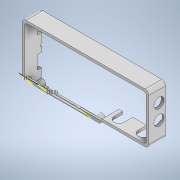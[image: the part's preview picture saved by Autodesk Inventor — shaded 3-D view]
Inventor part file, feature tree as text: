
AUTODESK INVENTOR PART (.ipt)
format: ipt  version: 2021 (Build 250183000, 183)  size: 572,928 bytes
history: native  units: mm
features: sketch x26, extrude x24, fillet x5, chamfer x5, hole x1
ambient origin geometry x8: Origin, YZ Plane, XZ Plane, XY Plane, X Axis, Y Axis, Z Axis, Center Point
bodies: Solid1 (feature_tree)
feature tree (61):
  extrude  "Extrusion1"  Depth=100.0mm
  extrude  "Extrusion3"  Depth=50.0mm
  extrude  "Extrusion4"  Depth=12.5mm
  extrude  "Extrusion12"  Depth=3.0mm TaperAngle=0.0deg
  extrude  "Extrusion13"  Depth=3.0mm TaperAngle=0.0deg
  fillet  "Fillet3"  Radius=2.0mm
  extrude  "Extrusion15"  Depth=2.0mm
  extrude  "Extrusion20"  Depth=1.2mm
  extrude  "Extrusion21"  Depth=12.0mm TaperAngle=0.0deg
  extrude  "Extrusion22"  Depth=2.0mm
  extrude  "Extrusion23"  Depth=3.0mm
  extrude  "Extrusion26"  Depth=4.4mm TaperAngle=0.0deg
  hole  "Hole2"  [1 undecoded]
  chamfer  "Chamfer6"  Distance=12.0mm
  chamfer  "Chamfer7"  Distance=12.0mm
  extrude  "Extrusion27"  Depth=8.0mm
  fillet  "Fillet4"  Radius=8.0mm
  extrude  "Extrusion28"  Depth=2.0mm TaperAngle=0.0deg
  extrude  "Extrusion29"  Depth=12.0mm
  extrude  "Extrusion30"  Depth=8.0mm
  fillet  "Fillet5"  Radius=8.0mm
  extrude  "Extrusion34"  Depth=2.0mm TaperAngle=0.0deg
  extrude  "Extrusion35"  Depth=3.0mm
  extrude  "Extrusion36"  Depth=50.0mm
  extrude  "Extrusion37"  Depth=3.0mm
  fillet  "Fillet6"  Radius=3.0mm
  extrude  "Extrusion38"  Depth=3.0mm
  extrude  "Extrusion39"  Depth=4.8mm
  chamfer  "Chamfer8"  Distance=6.0mm
  extrude  "Extrusion40"  Depth=2.0mm TaperAngle=45.0deg
  fillet  "Fillet7"  Radius=0.8mm
  extrude  "Extrusion41"  Depth=0.5mm
  chamfer  "Chamfer9"  Distance=2.0mm
  chamfer  "Chamfer10"  Distance=2.0mm
  extrude  "Extrusion42"  Depth=2.0mm
  sketch  "Sketch47"  dims[d158=4.8mm d159=6.0mm d160=0.0mm d161=2.0mm d162=6.0mm d163=4.0mm d164=2.0mm d165=90.0deg d166=4.0mm d167=20.594885mm d177=2.0mm d178=2.0mm d179=45.0deg d180=0.8mm d181=2.0mm d182=45.0deg d184=68.0mm d189=2.0mm d190=0.0mm d191=2.0mm d192=2.0mm d193=24.0mm d194=2.0mm d195=0.0mm d196=36.5mm d197=46.5mm d198=3.5mm d199=2.0mm d200=0.0mm d201=12.5mm d202=23.0mm d203=3.5mm d204=2.0mm d205=0.0mm d206=1.0mm d217=7.6mm d218=10.0mm d219=46.4mm d220=20.0mm d221=0.0mm d222=22.68928mm d223=67.0mm d224=0.0mm d225=1.2mm d226=0.0mm d227=1.2mm d228=0.0mm d229=3.0mm d230=12.3mm d231=33.2mm d232=1.0mm d233=10.0mm d234=1.2mm d235=0.0mm d236=1.2mm d237=5.0mm d238=20.0mm d239=1.5mm d240=0.0mm d241=1.5mm d242=2.0mm d243=45.0deg d245=1.2mm d246=0.0mm d247=2.0mm d248=5.0mm d249=0.0mm d250=0.8mm d251=2.0mm d252=45.0deg d253=0.6mm d254=2.0mm d255=45.0deg d256=5.0mm d257=0.0mm d258=2.0mm d259=0.0mm d262=12.0mm d263=33.2mm d67=0.5mm d68=0.872665mm d69=0.5mm d70=0.872665mm d71=0.5mm d72=0.872665mm d73=0.5mm d74=0.872665mm d75=0.872665mm d76=0.5mm d77=0.872665mm d208=0.5mm d209=0.872665mm d210=0.5mm d211=0.872665mm d264=0.5mm d265=0.872665mm]
  sketch  "Sketch1"  dims[d0=52.0mm d1=100.0mm]
  sketch  "Sketch4"  dims[d2=26.0mm d3=50.0mm]
  sketch  "Sketch5"  dims[d4=1.2mm d5=0.0mm d35=12.5mm]
  sketch  "Sketch13"  dims[d36=63.1mm d37=3.0mm d38=0.0mm]
  sketch  "Sketch14"  dims[d39=50.673mm d40=3.0mm d41=0.0mm d79=2.0mm]
  sketch  "Sketch16"  dims[d80=2.0mm d81=2.0mm]
  sketch  "Sketch21"  dims[d82=1.2mm d83=44.0mm]
  sketch  "Sketch22"  dims[d84=59.0mm d85=12.0mm d86=0.0mm]
  sketch  "Sketch23"  dims[d87=2.0mm d88=12.6mm]
  sketch  "Sketch24"  dims[d89=12.0mm d90=0.0mm d91=3.0mm]
  sketch  "Sketch27"  dims[d95=33.8mm d96=4.4mm d97=0.0mm]
  sketch  "Sketch28"  dims[d117=2.0mm d118=2.0mm d119=12.0mm d120=0.0mm d121=12.0mm d122=0.0mm]
  sketch  "Sketch29"  dims[d123=70.0mm d124=89.0mm d125=8.0mm]
  sketch  "Sketch30"  dims[d126=8.0mm d127=2.0mm d128=0.0mm]
  sketch  "Sketch31"  dims[d129=8.0mm d130=12.0mm]
  sketch  "Sketch32"  dims[d131=12.0mm d132=8.0mm d133=8.0mm]
  sketch  "Sketch36"  dims[d134=8.0mm d135=2.0mm d136=0.0mm]
  sketch  "Sketch37"  dims[d144=3.0mm d145=3.0mm]
  sketch  "Sketch38"  dims[d146=3.0mm d147=50.0mm]
  sketch  "Sketch39"  dims[d148=97.0mm d149=15.0mm d150=3.0mm]
  sketch  "Sketch40"  dims[d151=3.0mm d152=97.0mm]
  sketch  "Sketch41"  dims[d153=49.0mm d154=4.8mm]
  sketch  "Sketch43"  dims[d155=4.8mm]
  sketch  "Sketch44"  dims[d156=4.8mm]
  sketch  "Sketch45"  dims[d157=4.8mm]
note: 1 required parameter value undecoded (feature->parameter linkage not recoverable at this tier; creation-order binding heuristic only, values carry confidence <= 0.55)
